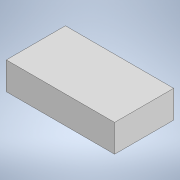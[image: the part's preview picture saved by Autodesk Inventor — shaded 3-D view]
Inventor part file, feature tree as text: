
AUTODESK INVENTOR PART (.ipt)
format: ipt  version: 2020 (Build 240168000, 168)  size: 87,040 bytes
history: native  units: mm
features: extrude x1, sketch x1
ambient origin geometry x8: Origin, YZ Plane, XZ Plane, XY Plane, X Axis, Y Axis, Z Axis, Center Point
bodies: Solid1 (feature_tree)
feature tree (2):
  extrude  "Extrusion1"  Depth=30.0mm
  sketch  "Sketch1"  dims[d0=55.0mm d1=30.0mm d2=14.0mm d3=0.0mm]
